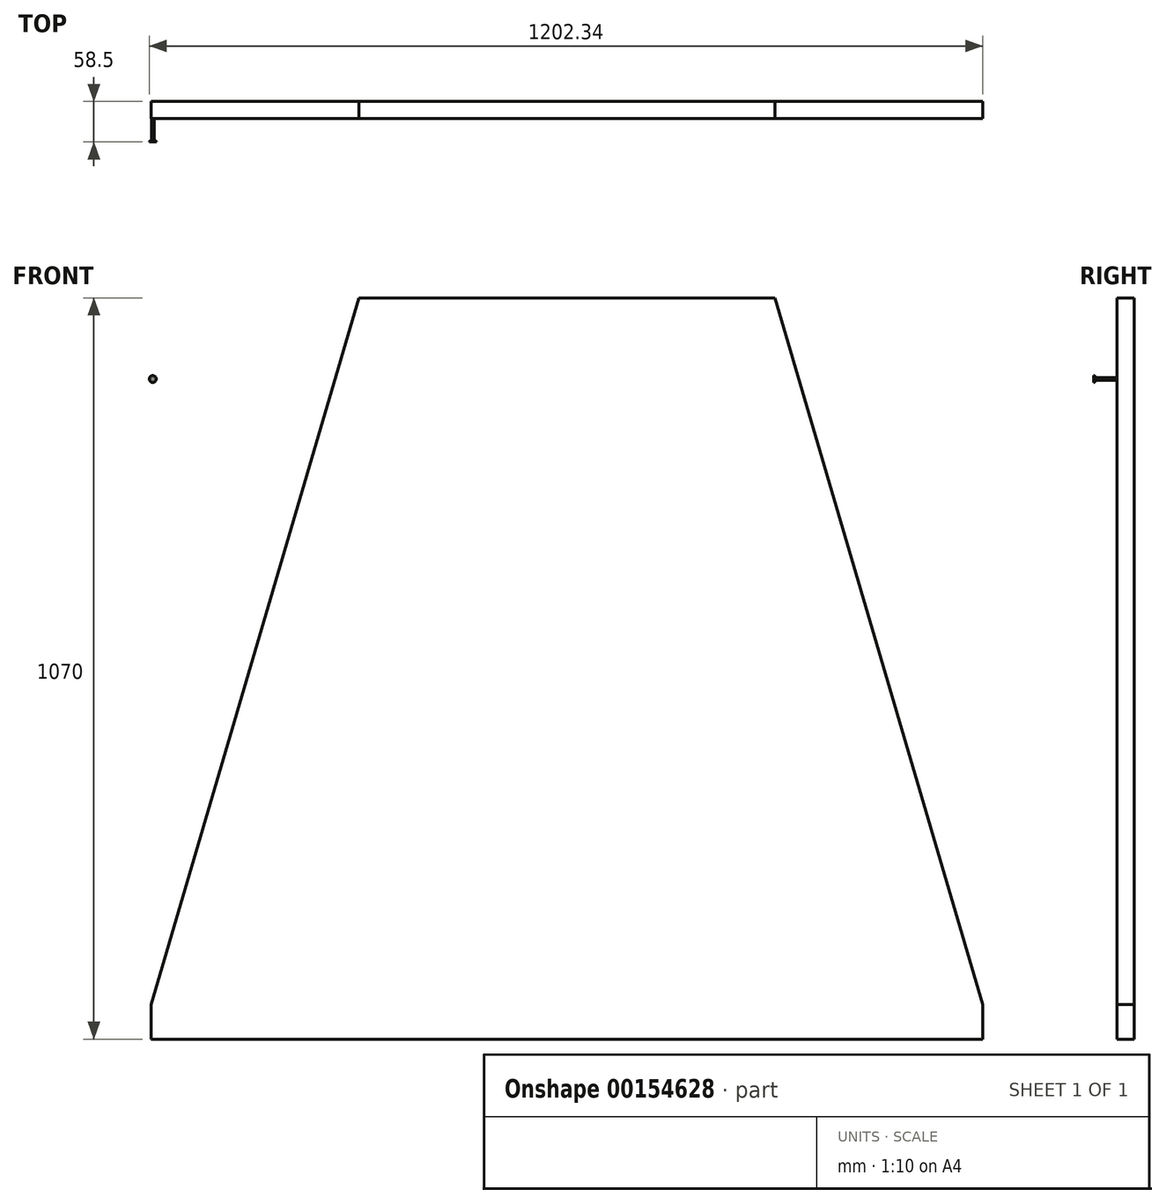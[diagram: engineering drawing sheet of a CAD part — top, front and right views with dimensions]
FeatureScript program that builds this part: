
annotation { "Feature Type Name" : "Feature", "Feature Type Description" : "" }
export const myFeature = defineFeature(function(context is Context, id is Id, definition is map)
    precondition{}
    {
        {
            assignVariable(context, id + "F0", {"name" : "Thickness", "anyValue" : 25 * mm});
        }
        {
            assignVariable(context, id + "F1", {"name" : "ScrewLength", "anyValue" : 30 * mm});
        }
        {
            var Q0;
            Q0=qCreatedBy(makeId("Front.planeOp"),FACE);
            var sketch = newSketch(context, id + "F2", { "sketchPlane" : qUnion([Q0])});
            skLineSegment(sketch, "E0.bottom", {"start": v(600, 0) * mm, "end": v(-600, 0) * mm});
            skLineSegment(sketch, "E1", {"start": v(-600, 25) * mm, "end": v(600, 25) * mm, "construction": true});
            skLineSegment(sketch, "E2", {"start": v(0, 1070) * mm, "end": v(0, 0) * mm, "construction": true});
            skCircle(sketch, "E3", {"center": v(-597.34, 952.85) * mm, "radius": 2 * mm});
            skPoint(sketch, "E4", {"position": v(25, 25) * mm});
            skPoint(sketch, "E5.1.0.0", {"position": v(75, 25) * mm});
            skPoint(sketch, "E5.2.0.0", {"position": v(125, 25) * mm});
            skPoint(sketch, "E5.3.0.0", {"position": v(175, 25) * mm});
            skPoint(sketch, "E5.4.0.0", {"position": v(225, 25) * mm});
            skPoint(sketch, "E5.5.0.0", {"position": v(275, 25) * mm});
            skPoint(sketch, "E5.6.0.0", {"position": v(325, 25) * mm});
            skPoint(sketch, "E5.7.0.0", {"position": v(375, 25) * mm});
            skPoint(sketch, "E5.8.0.0", {"position": v(425, 25) * mm});
            skPoint(sketch, "E5.9.0.0", {"position": v(475, 25) * mm});
            skPoint(sketch, "E5.10.0.0", {"position": v(525, 25) * mm});
            skPoint(sketch, "E5.11.0.0", {"position": v(575, 25) * mm});
            skLineSegment(sketch, "E5.direction1", {"start": v(25, 25) * mm, "end": v(75, 25) * mm, "construction": true});
            skPoint(sketch, "E6.MirrorP", {"position": v(-25, 25) * mm});
            skPoint(sketch, "E7.1.0.0", {"position": v(-75, 25) * mm});
            skPoint(sketch, "E7.2.0.0", {"position": v(-125, 25) * mm});
            skPoint(sketch, "E7.3.0.0", {"position": v(-175, 25) * mm});
            skPoint(sketch, "E7.4.0.0", {"position": v(-225, 25) * mm});
            skPoint(sketch, "E7.5.0.0", {"position": v(-275, 25) * mm});
            skPoint(sketch, "E7.6.0.0", {"position": v(-325, 25) * mm});
            skPoint(sketch, "E7.7.0.0", {"position": v(-375, 25) * mm});
            skPoint(sketch, "E7.8.0.0", {"position": v(-425, 25) * mm});
            skPoint(sketch, "E7.9.0.0", {"position": v(-475, 25) * mm});
            skPoint(sketch, "E7.10.0.0", {"position": v(-525, 25) * mm});
            skPoint(sketch, "E7.11.0.0", {"position": v(-575, 25) * mm});
            skLineSegment(sketch, "E7.direction1", {"start": v(-25, 25) * mm, "end": v(-75, 25) * mm, "construction": true});
            skPoint(sketch, "E8", {"position": v(0, 1045) * mm});
            skLineSegment(sketch, "E9.top", {"start": v(300, 1070) * mm, "end": v(-300, 1070) * mm});
            skLineSegment(sketch, "E10", {"start": v(-307.35, 1045) * mm, "end": v(307.35, 1045) * mm, "construction": true});
            skPoint(sketch, "E11", {"position": v(260, 1045) * mm});
            skPoint(sketch, "E12.MirrorP", {"position": v(-260, 1045) * mm});
            skLineSegment(sketch, "E13", {"start": v(-300, 1070) * mm, "end": v(-600, 50) * mm});
            skLineSegment(sketch, "E14", {"start": v(300, 1070) * mm, "end": v(600, 50) * mm});
            skLineSegment(sketch, "E15", {"start": v(-600, 50) * mm, "end": v(-600, 0) * mm});
            skLineSegment(sketch, "E16", {"start": v(600, 50) * mm, "end": v(600, 0) * mm});
            skSolve(sketch);
        }
        {
            var Q0;
            Q0=makeQuery(id+"F2.imprint","IMPRINT",FACE,{"disambiguationData":[TD([[makeQuery(id+"F2.imprint","IMPRINT",EDGE,{"derivedFrom":sQuery(id+"F2.wireOp",EDGE,"E0.bottom")}),-1.0]])]});
            extrude(context, id + "F3", {"entities" : qUnion([Q0]), "oppositeDirection" : true, "depth" : getVariable(context, 'Thickness')});
        }
        {
            var Q0;
            Q0=makeQuery(id+"F2.imprint","IMPRINT",FACE,{"disambiguationData":[TD([[makeQuery(id+"F2.imprint","IMPRINT",EDGE,{"derivedFrom":sQuery(id+"F2.wireOp",EDGE,"E3")}),1.0]])]});
            var Q1;
            Q1=sQuery(id+"F2.wireOp",EDGE,"E3");
            extrude(context, id + "F4", {"entities" : qUnion([Q0]), "surfaceEntities" : qUnion([Q1]), "depth" : getVariable(context, 'ScrewLength')});
        }
        {
            var Q0;
            Q0=makeQuery(id+"F4.opExtrude","CAP_FACE",FACE,{"disambiguationData":[OSD([sQuery(id+"F2.wireOp",EDGE,"E3")])],"isStart":false});
            extrude(context, id + "F5", {"entities" : qUnion([Q0]), "operationType" : NewBodyOperationType.ADD, "depth" : 3 * mm, "hasDraft" : true, "draftAngle" : 45 * degree});
        }
        {
            var Q0;
            Q0=makeQuery(id+"F5.opExtrude","CAP_FACE",FACE,{"disambiguationData":[OSD([sQuery(id+"F2.wireOp",EDGE,"E3")])],"isStart":false});
            extrude(context, id + "F6", {"entities" : qUnion([Q0]), "operationType" : NewBodyOperationType.ADD, "depth" : 0.5 * mm});
        }
    });
